# Revit family: Haworth_BuzziSpark_Sofa_TwoSeats
name_source: partatom
category: Furniture
revit_build: Autodesk Revit 2018 (Build: 20170223_1515(x64)
units: mm (PartAtom-declared; Revit-internal decimal feet)

## family parameters
Always vertical = Yes
Cut with Voids When Loaded = No
OmniClass Number = 23.40.70.14.64.21
OmniClass Title = Systems Furniture
Room Calculation Point = No
Shared = No
Work Plane-Based = No

## types (3) — shared parameters
Actual Depth = 37.52 "
Actual Width = 94.09 "
Arm Offset = 5.52 "
Assembly Code = E2020200
Back Cushion Offset = 19.81 "
Back Cushion Width = 38.63 "
Back Upholstery Width = 43.65 "
Manufacturer = Haworth
Middle Leg Control = No
Model = HCBZ-SKL2
Revision Number = 1
Seat Depth = 27.56 "
Seat Height = 17.72 "
Seat Offset = 21.82 "
Seat Width = 50.51 "
Shield Width = 45.28 "
Shield w Tube Thickness = 3.4 "
Side Upholstery Width = 25.5 "
Size = Verify Final Dim. w/ Haworth
URL = https://www.haworth.com
URL - Product = https://www.haworth.com
Warranty = http://www.haworth.com
With Arm Cushion = Yes

## per-type parameters (varying)
| type | Description | Shield 1 Height | Shield 2 Height |
| HCBZ-SKL2 - High Back | Haworth BuzziSpark Two Seat Sofa High Back | Haworth_BuzziSpark_Sofa_ShieldUpholstery_Part : High | Haworth_BuzziSpark_Sofa_ShieldUpholstery_Part : High |
| HCBZ-SKL2 - Medium Back | Haworth BuzziSpark Two Seat Sofa Medium Back | Haworth_BuzziSpark_Sofa_ShieldUpholstery_Part : Medium | Haworth_BuzziSpark_Sofa_ShieldUpholstery_Part : Medium |
| HCBZ-SKL2 - Medium Back - High Back | Haworth BuzziSpark Two Seat Sofa Medium-High Back | Haworth_BuzziSpark_Sofa_ShieldUpholstery_Part : Medium | Haworth_BuzziSpark_Sofa_ShieldUpholstery_Part : High |

## geometry (parser evidence)
native form markers: Extrusion x2, Sweep x14
no freeform markers — native parametric forms only
